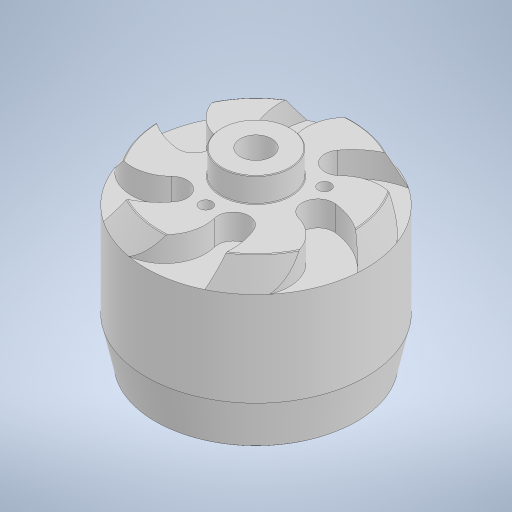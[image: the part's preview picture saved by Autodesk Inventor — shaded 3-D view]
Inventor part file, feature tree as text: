
AUTODESK INVENTOR PART (.ipt)
format: ipt  version: 2023.2 (Build 272271000, 271)  size: 348,672 bytes
history: native  units: in
note: dims shown in document units (in); Inventor stores cm internally (conversion verified against a paired STEP export)
features: sketch x2, revolve x1, chamfer x1, extrude x1
ambient origin geometry x8: Origin, YZ Plane, XZ Plane, XY Plane, X Axis, Y Axis, Z Axis, Center Point
bodies: Solid1 (feature_tree)
feature tree (5):
  revolve  "Revolution1"  [1 undecoded]
  chamfer  "Chamfer1"  Distance=0.2756in
  extrude  "Extrusion1"  Depth=0.4528in
  sketch  "Sketch1"  dims[d0=1.1772in d1=0.6299in]
  sketch  "Sketch2"  dims[d2=0.689in d3=0.2756in d4=0.8661in d5=0.6004in d6=0.1575in d7=0.2165in d8=0.0984in d9=90.0deg d10=0.0039in d11=0.125in d12=45.0deg d13=0.6299in d14=0.0787in d15=1.1811in d17=360.0deg d19=0.5807in d21=0.1969in d22=1.378in d23=1.2008in d24=0.1969in d26=30.0deg d27=0.2559in d28=0.4528in d29=2.3622in d31=360.0deg d33=0.1575in d34=0.0in]
note: 1 required parameter value undecoded (feature->parameter linkage not recoverable at this tier; creation-order binding heuristic only, values carry confidence <= 0.55)
